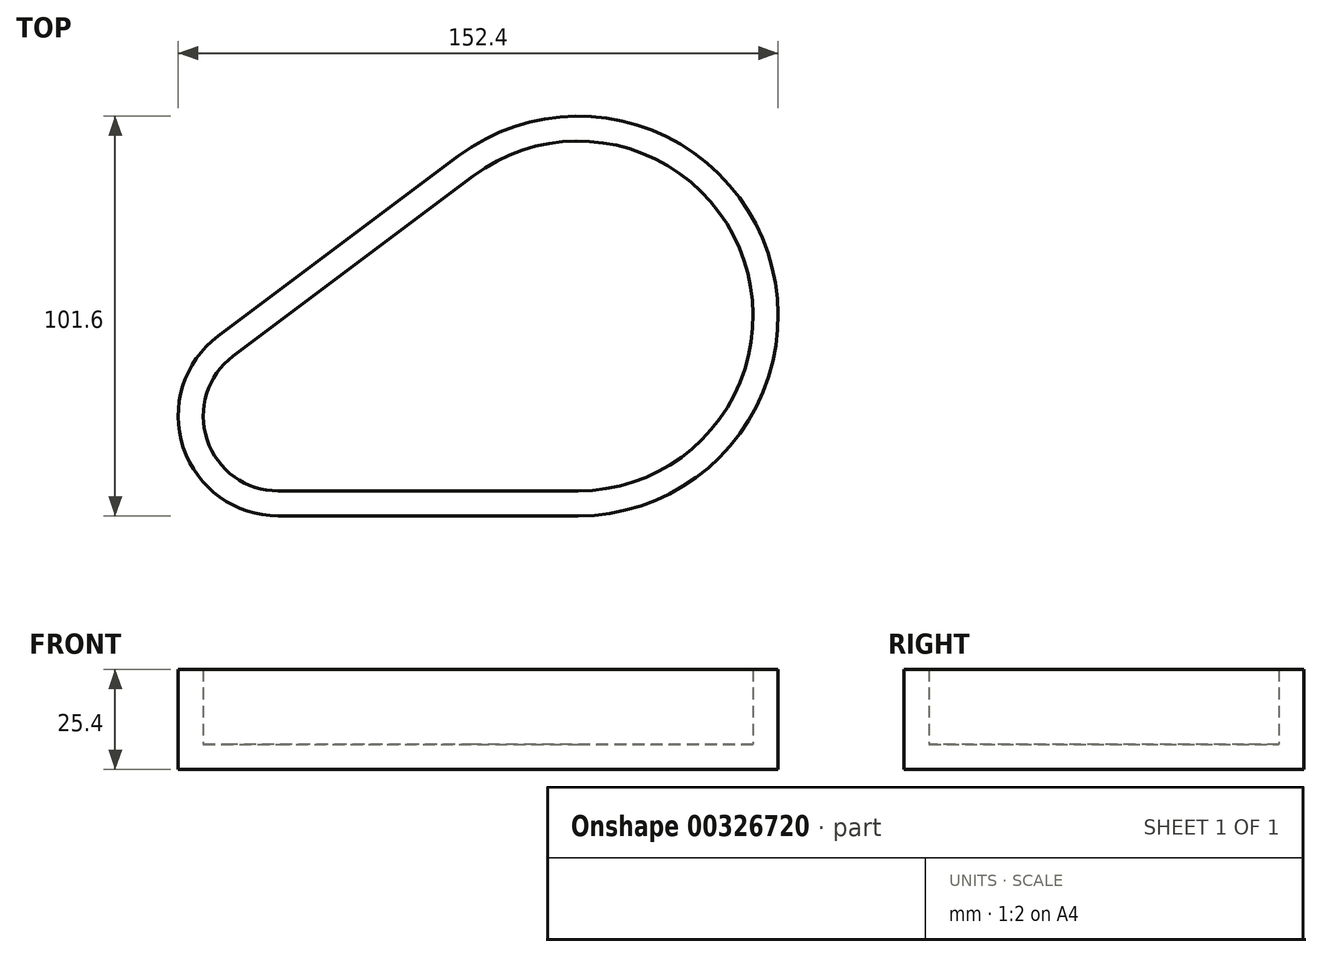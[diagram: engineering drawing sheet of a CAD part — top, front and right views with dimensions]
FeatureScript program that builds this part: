
annotation { "Feature Type Name" : "Feature", "Feature Type Description" : "" }
export const myFeature = defineFeature(function(context is Context, id is Id, definition is map)
    precondition{}
    {
        {
            var Q0;
            Q0=qCreatedBy(makeId("Top.planeOp"),FACE);
            var sketch = newSketch(context, id + "F0", { "sketchPlane" : qUnion([Q0])});
            skArc(sketch, "E0", {"start": v(10.16, 45.72) * mm, "mid": v(1.3, 17.37) * mm, "end": v(25.4, 0) * mm});
            skArc(sketch, "E1", {"start": v(101.6, 0) * mm, "mid": v(149.8, 66.86) * mm, "end": v(71.12, 91.44) * mm});
            skLineSegment(sketch, "E2", {"start": v(25.4, 0) * mm, "end": v(101.6, 0) * mm});
            skLineSegment(sketch, "E3", {"start": v(10.16, 45.72) * mm, "end": v(71.12, 91.44) * mm});
            skSolve(sketch);
        }
        {
            var Q0;
            Q0=makeQuery(id+"F0.imprint","IMPRINT",FACE,{"disambiguationData":[TD([[makeQuery(id+"F0.imprint","IMPRINT",EDGE,{"derivedFrom":sQuery(id+"F0.wireOp",EDGE,"E0")}),1.0]])]});
            extrude(context, id + "F1", {"entities" : qUnion([Q0]), "depth" : 6.35 * mm});
        }
        {
            var Q0;
            Q0=makeQuery(id+"F1.opExtrude","CAP_FACE",FACE,{"disambiguationData":[OSD([sQuery(id+"F0.wireOp",EDGE,"E0"),sQuery(id+"F0.wireOp",EDGE,"E1"),sQuery(id+"F0.wireOp",EDGE,"E2"),sQuery(id+"F0.wireOp",EDGE,"E3")])],"isStart":false});
            var sketch = newSketch(context, id + "F2", { "sketchPlane" : qUnion([Q0])});
            skSolve(sketch);
        }
        {
            var Q0;
            Q0=makeQuery(id+"F2.imprint","IMPRINT",FACE,{"disambiguationData":[TD([[makeQuery(id+"F2.imprint","IMPRINT",EDGE,{"derivedFrom":makeQuery(id+"F1.opExtrude","CAP_EDGE",EDGE,{"disambiguationData":[OSD([sQuery(id+"F0.wireOp",EDGE,"E0")])],"isStart":false})}),1.0]])]});
            var sketch = newSketch(context, id + "F3", { "sketchPlane" : qUnion([Q0])});
            skArc(sketch, "E4.0.0", {"start": v(10.16, 45.72) * mm, "mid": v(1.3, 17.37) * mm, "end": v(25.4, 0) * mm});
            skLineSegment(sketch, "E4.0.1", {"start": v(25.4, 0) * mm, "end": v(101.6, 0) * mm});
            skArc(sketch, "E4.0.2", {"start": v(101.6, 0) * mm, "mid": v(149.8, 66.86) * mm, "end": v(71.12, 91.44) * mm});
            skLineSegment(sketch, "E4.0.3", {"start": v(71.12, 91.44) * mm, "end": v(10.16, 45.72) * mm});
            skArc(sketch, "E5.0", {"start": v(13.97, 40.64) * mm, "mid": v(7.33, 19.38) * mm, "end": v(25.4, 6.35) * mm});
            skLineSegment(sketch, "E5.1", {"start": v(74.93, 86.36) * mm, "end": v(13.97, 40.64) * mm});
            skArc(sketch, "E5.2", {"start": v(101.6, 6.35) * mm, "mid": v(143.77, 64.86) * mm, "end": v(74.93, 86.36) * mm});
            skLineSegment(sketch, "E5.3", {"start": v(25.4, 6.35) * mm, "end": v(101.6, 6.35) * mm});
            skSolve(sketch);
        }
        {
            var Q0;
            Q0 = qSketchRegion(id + "F3", true);
            extrude(context, id + "F4", {"entities" : qUnion([Q0]), "operationType" : NewBodyOperationType.ADD, "depth" : 19.05 * mm});
        }
    });
